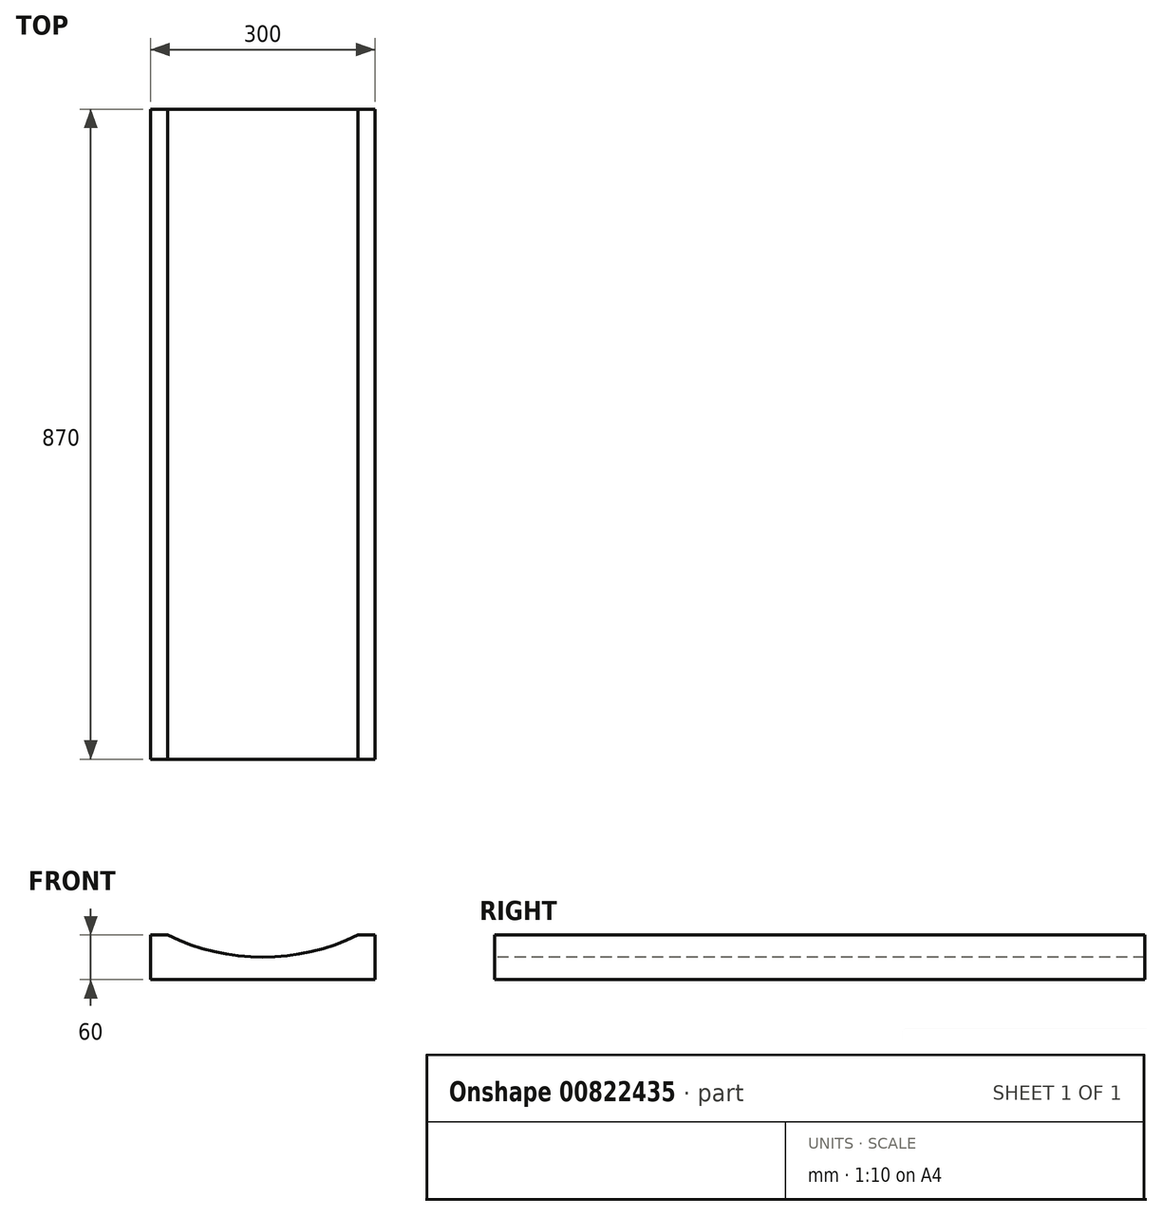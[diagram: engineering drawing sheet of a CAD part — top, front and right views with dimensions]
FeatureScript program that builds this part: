
annotation { "Feature Type Name" : "Feature", "Feature Type Description" : "" }
export const myFeature = defineFeature(function(context is Context, id is Id, definition is map)
    precondition{}
    {
        {
            var Q0;
            Q0=qCreatedBy(makeId("Front.planeOp"),FACE);
            var sketch = newSketch(context, id + "F0", { "sketchPlane" : qUnion([Q0])});
            skLineSegment(sketch, "E0", {"start": v(-127.28, 0) * mm, "end": v(-150, 0) * mm});
            skLineSegment(sketch, "E1", {"start": v(-150, 0) * mm, "end": v(-150, -60) * mm});
            skLineSegment(sketch, "E2", {"start": v(-150, -60) * mm, "end": v(150, -60) * mm});
            skLineSegment(sketch, "E3", {"start": v(150, -60) * mm, "end": v(150, 0) * mm});
            skLineSegment(sketch, "E4", {"start": v(150, 0) * mm, "end": v(127.28, 0) * mm});
            skLineSegment(sketch, "E5", {"start": v(0, 0) * mm, "end": v(0, 255) * mm, "construction": true});
            skArc(sketch, "E6", {"start": v(-127.28, 0) * mm, "mid": v(0, -30) * mm, "end": v(127.28, 0) * mm});
            skSolve(sketch);
        }
        {
            var Q0;
            Q0 = qSketchRegion(id + "F0", true);
            extrude(context, id + "F1", {"entities" : qUnion([Q0]), "oppositeDirection" : true, "depth" : 870 * mm, "offsetDistance" : 25 * mm});
        }
    });
